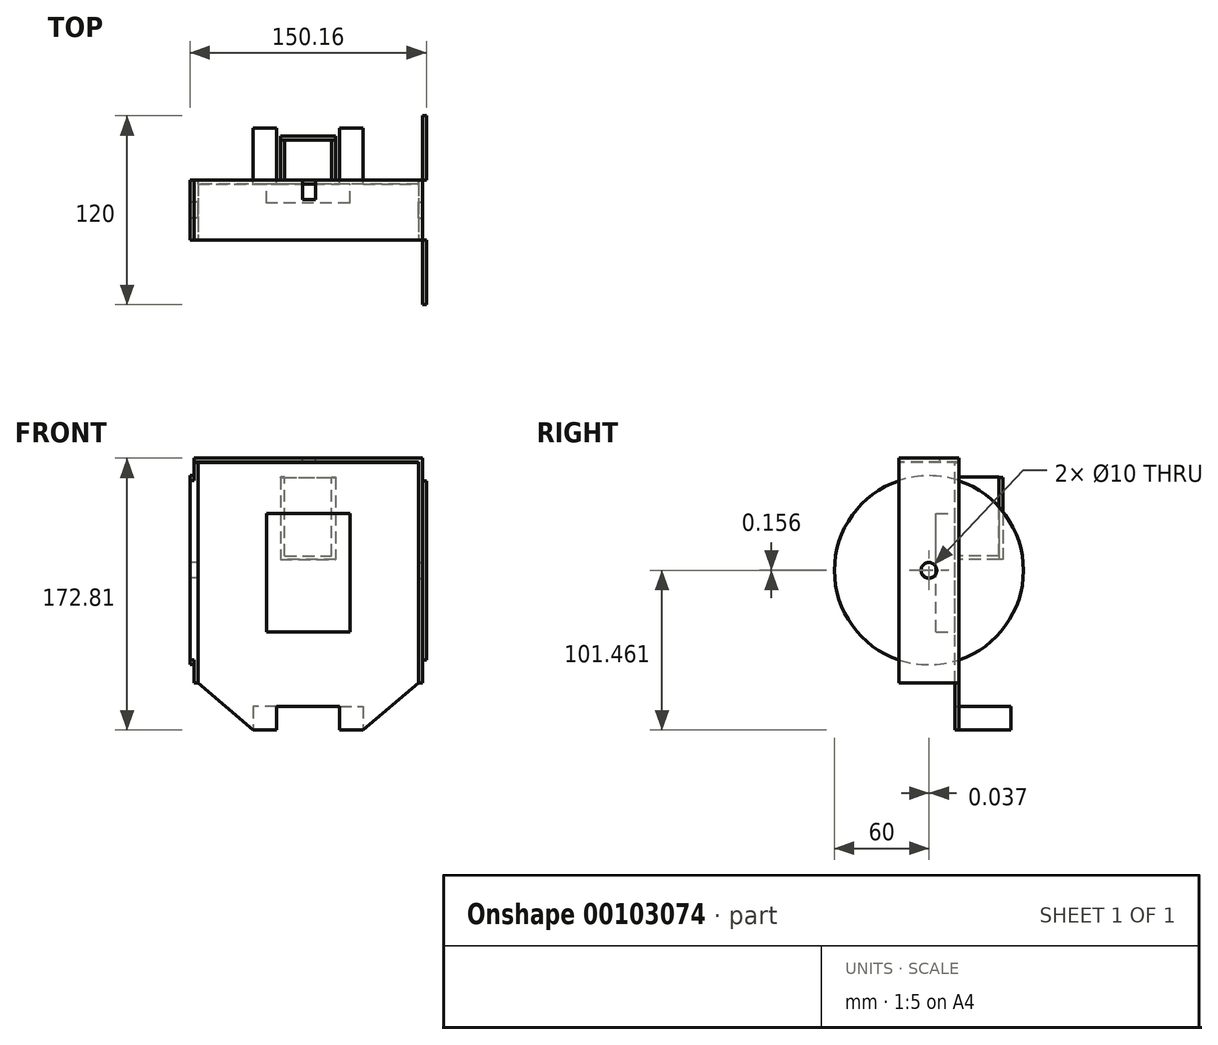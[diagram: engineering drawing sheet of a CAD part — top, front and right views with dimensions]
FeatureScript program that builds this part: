
annotation { "Feature Type Name" : "Feature", "Feature Type Description" : "" }
export const myFeature = defineFeature(function(context is Context, id is Id, definition is map)
    precondition{}
    {
        {
            var Q0;
            Q0=qCreatedBy(makeId("Front.planeOp"),FACE);
            var sketch = newSketch(context, id + "F0", { "sketchPlane" : qUnion([Q0])});
            skLineSegment(sketch, "E0.bottom", {"start": v(35, -85) * mm, "end": v(20, -85) * mm});
            skLineSegment(sketch, "E0.top", {"start": v(70, 85) * mm, "end": v(-70, 85) * mm});
            skLineSegment(sketch, "E0.left", {"start": v(70, -55) * mm, "end": v(70, 85) * mm});
            skLineSegment(sketch, "E0.right", {"start": v(-70, -55) * mm, "end": v(-70, 85) * mm});
            skPoint(sketch, "E0.middle", {"position": v(0, 0) * mm});
            skLineSegment(sketch, "E1", {"start": v(-70, -55) * mm, "end": v(-35, -85) * mm});
            skLineSegment(sketch, "E2", {"start": v(35, -85) * mm, "end": v(70, -55) * mm});
            skPoint(sketch, "E3.orphan", {"position": v(-70, -85) * mm});
            skPoint(sketch, "E4.orphan", {"position": v(70, -85) * mm});
            skLineSegment(sketch, "E5", {"start": v(-35, -85) * mm, "end": v(-20, -85) * mm});
            skLineSegment(sketch, "E6", {"start": v(-20, -85) * mm, "end": v(-20, -70) * mm});
            skLineSegment(sketch, "E7", {"start": v(20, -85) * mm, "end": v(20, -70) * mm});
            skLineSegment(sketch, "E8", {"start": v(-20, -70) * mm, "end": v(20, -70) * mm});
            skLineSegment(sketch, "E9.trimOffspring", {"start": v(-20, -85) * mm, "end": v(-35, -85) * mm});
            skSolve(sketch);
        }
        {
            var Q0;
            Q0=makeQuery(id+"F0.imprint","IMPRINT",FACE,{"disambiguationData":[TD([[makeQuery(id+"F0.imprint","IMPRINT",EDGE,{"derivedFrom":sQuery(id+"F0.wireOp",EDGE,"E0.top")}),1.0]])]});
            extrude(context, id + "F1", {"entities" : qUnion([Q0]), "depth" : 2.54 * mm});
        }
        {
            var Q0;
            Q0=makeQuery(id+"F1.opExtrude","CAP_FACE",FACE,{"disambiguationData":[OSD([sQuery(id+"F0.wireOp",EDGE,"E0.top"),sQuery(id+"F0.wireOp",EDGE,"E0.left"),sQuery(id+"F0.wireOp",EDGE,"E0.right"),sQuery(id+"F0.wireOp",EDGE,"E1"),sQuery(id+"F0.wireOp",EDGE,"E2"),sQuery(id+"F0.wireOp",EDGE,"E0.bottom"),sQuery(id+"F0.wireOp",EDGE,"E6"),sQuery(id+"F0.wireOp",EDGE,"E7"),sQuery(id+"F0.wireOp",EDGE,"E8"),sQuery(id+"F0.wireOp",EDGE,"E9.trimOffspring")])],"isStart":false});
            var sketch = newSketch(context, id + "F2", { "sketchPlane" : qUnion([Q0])});
            skLineSegment(sketch, "E10.bottom", {"start": v(26.5, -22.5) * mm, "end": v(-26.5, -22.5) * mm});
            skLineSegment(sketch, "E10.top", {"start": v(26.5, 52.5) * mm, "end": v(-26.5, 52.5) * mm});
            skLineSegment(sketch, "E10.left", {"start": v(26.5, -22.5) * mm, "end": v(26.5, 52.5) * mm});
            skLineSegment(sketch, "E10.right", {"start": v(-26.5, -22.5) * mm, "end": v(-26.5, 52.5) * mm});
            skPoint(sketch, "E10.middle", {"position": v(0, 15) * mm});
            skPoint(sketch, "E11.orphan", {"position": v(70, 85) * mm});
            skPoint(sketch, "E12.orphan", {"position": v(-70, -55) * mm});
            skSolve(sketch);
        }
        {
            var Q0;
            Q0=makeQuery(id+"F2.imprint","IMPRINT",FACE,{"disambiguationData":[TD([[makeQuery(id+"F2.imprint","IMPRINT",EDGE,{"derivedFrom":sQuery(id+"F2.wireOp",EDGE,"E10.bottom")}),-1.0]])]});
            extrude(context, id + "F3", {"entities" : qUnion([Q0]), "operationType" : NewBodyOperationType.ADD, "depth" : 12 * mm});
        }
        {
            var Q0;
            Q0=makeQuery(id+"F1.opExtrude","SWEPT_FACE",FACE,{"disambiguationData":[OSD([sQuery(id+"F0.wireOp",EDGE,"E0.right")])]});
            cPlane(context, id + "F4", {"entities" : qUnion([Q0]), "cplaneType" : CPlaneType.OFFSET, "offset" : 0 * mm, "width" : 152.4 * mm, "height" : 152.4 * mm});
        }
        {
            var Q0;
            Q0=qCreatedBy(id+"F4.planeOp",FACE);
            var sketch = newSketch(context, id + "F5", { "sketchPlane" : qUnion([Q0])});
            skLineSegment(sketch, "E13.bottom", {"start": v(0, 85.03) * mm, "end": v(38.1, 85.03) * mm});
            skLineSegment(sketch, "E13.top", {"start": v(0, -54.97) * mm, "end": v(38.1, -54.97) * mm});
            skLineSegment(sketch, "E13.left", {"start": v(0, 85.03) * mm, "end": v(0, -54.97) * mm});
            skLineSegment(sketch, "E13.right", {"start": v(38.1, 85.03) * mm, "end": v(38.1, -54.97) * mm});
            skSolve(sketch);
        }
        {
            var Q0;
            Q0=makeQuery(id+"F5.imprint","IMPRINT",FACE,{"disambiguationData":[TD([[makeQuery(id+"F5.imprint","IMPRINT",EDGE,{"derivedFrom":sQuery(id+"F5.wireOp",EDGE,"E13.bottom")}),-1.0]])]});
            extrude(context, id + "F6", {"entities" : qUnion([Q0]), "operationType" : NewBodyOperationType.ADD, "depth" : 2.54 * mm});
        }
        {
            var Q0;
            Q0=makeQuery(id+"F1.opExtrude","SWEPT_FACE",FACE,{"disambiguationData":[OSD([sQuery(id+"F0.wireOp",EDGE,"E0.left")])]});
            var Q1;
            Q1 = qBodyType(qCreatedBy(id + "F8" ,EDGE), BodyType.WIRE);
            cPlane(context, id + "F7", {"entities" : qUnion([Q0, Q1]), "cplaneType" : CPlaneType.OFFSET, "offset" : 0 * mm, "width" : 152.4 * mm, "height" : 152.4 * mm});
        }
        {
            var Q0;
            Q0=qCreatedBy(id+"F7.planeOp",FACE);
            var sketch = newSketch(context, id + "F8", { "sketchPlane" : qUnion([Q0])});
            skLineSegment(sketch, "E14.bottom", {"start": v(0, -54.89) * mm, "end": v(-38.1, -54.89) * mm});
            skLineSegment(sketch, "E14.top", {"start": v(0, 85.27) * mm, "end": v(-38.1, 85.27) * mm});
            skLineSegment(sketch, "E14.left", {"start": v(0, -54.89) * mm, "end": v(0, 85.27) * mm});
            skLineSegment(sketch, "E14.right", {"start": v(-38.1, -54.89) * mm, "end": v(-38.1, 85.27) * mm});
            skSolve(sketch);
        }
        {
            var Q0;
            Q0=makeQuery(id+"F8.imprint","IMPRINT",FACE,{"disambiguationData":[TD([[makeQuery(id+"F8.imprint","IMPRINT",EDGE,{"derivedFrom":sQuery(id+"F8.wireOp",EDGE,"E14.bottom")}),-1.0]])]});
            extrude(context, id + "F9", {"entities" : qUnion([Q0]), "operationType" : NewBodyOperationType.ADD, "depth" : 2.54 * mm});
        }
        {
            var Q0;
            Q0=makeQuery(id+"F9.boolean.opBoolean","MERGE",FACE,{"derivedFrom":[makeQuery(id+"F6.boolean.opBoolean","MERGE",FACE,{"derivedFrom":[makeQuery(id+"F1.opExtrude","CAP_FACE",FACE,{"disambiguationData":[OSD([sQuery(id+"F0.wireOp",EDGE,"E0.top"),sQuery(id+"F0.wireOp",EDGE,"E0.left"),sQuery(id+"F0.wireOp",EDGE,"E0.right"),sQuery(id+"F0.wireOp",EDGE,"E1"),sQuery(id+"F0.wireOp",EDGE,"E2"),sQuery(id+"F0.wireOp",EDGE,"E0.bottom"),sQuery(id+"F0.wireOp",EDGE,"E6"),sQuery(id+"F0.wireOp",EDGE,"E7"),sQuery(id+"F0.wireOp",EDGE,"E8"),sQuery(id+"F0.wireOp",EDGE,"E9.trimOffspring")])],"isStart":true}),makeQuery(id+"F6.opExtrude","SWEPT_FACE",FACE,{"disambiguationData":[OSD([sQuery(id+"F5.wireOp",EDGE,"E13.left")])]})]}),makeQuery(id+"F9.opExtrude","SWEPT_FACE",FACE,{"disambiguationData":[OSD([sQuery(id+"F8.wireOp",EDGE,"E14.left")])]})]});
            var sketch = newSketch(context, id + "F10", { "sketchPlane" : qUnion([Q0])});
            skLineSegment(sketch, "E15.bottom", {"start": v(-72.54, 85.27) * mm, "end": v(72.54, 85.27) * mm});
            skLineSegment(sketch, "E15.top", {"start": v(-72.54, 87.81) * mm, "end": v(72.54, 87.81) * mm});
            skLineSegment(sketch, "E15.left", {"start": v(-72.54, 85.27) * mm, "end": v(-72.54, 87.81) * mm});
            skLineSegment(sketch, "E15.right", {"start": v(72.54, 85.27) * mm, "end": v(72.54, 87.81) * mm});
            skSolve(sketch);
        }
        {
            var Q0;
            Q0=makeQuery(id+"F10.imprint","IMPRINT",FACE,{"disambiguationData":[TD([[makeQuery(id+"F10.imprint","IMPRINT",EDGE,{"derivedFrom":sQuery(id+"F10.wireOp",EDGE,"E15.top")}),-1.0]])]});
            extrude(context, id + "F11", {"entities" : qUnion([Q0]), "operationType" : NewBodyOperationType.ADD, "oppositeDirection" : true, "depth" : 38.1 * mm});
        }
        {
            var Q0;
            Q0=makeQuery(id+"F11.boolean.opBoolean","MERGE",FACE,{"derivedFrom":[makeQuery(id+"F9.boolean.opBoolean","MERGE",FACE,{"derivedFrom":[makeQuery(id+"F6.boolean.opBoolean","MERGE",FACE,{"derivedFrom":[makeQuery(id+"F1.opExtrude","CAP_FACE",FACE,{"disambiguationData":[OSD([sQuery(id+"F0.wireOp",EDGE,"E0.top"),sQuery(id+"F0.wireOp",EDGE,"E0.left"),sQuery(id+"F0.wireOp",EDGE,"E0.right"),sQuery(id+"F0.wireOp",EDGE,"E1"),sQuery(id+"F0.wireOp",EDGE,"E2"),sQuery(id+"F0.wireOp",EDGE,"E0.bottom"),sQuery(id+"F0.wireOp",EDGE,"E6"),sQuery(id+"F0.wireOp",EDGE,"E7"),sQuery(id+"F0.wireOp",EDGE,"E8"),sQuery(id+"F0.wireOp",EDGE,"E9.trimOffspring")])],"isStart":true}),makeQuery(id+"F6.opExtrude","SWEPT_FACE",FACE,{"disambiguationData":[OSD([sQuery(id+"F5.wireOp",EDGE,"E13.left")])]})]}),makeQuery(id+"F9.opExtrude","SWEPT_FACE",FACE,{"disambiguationData":[OSD([sQuery(id+"F8.wireOp",EDGE,"E14.left")])]})]}),makeQuery(id+"F11.opExtrude","CAP_FACE",FACE,{"disambiguationData":[OSD([sQuery(id+"F10.wireOp",EDGE,"E15.bottom"),sQuery(id+"F10.wireOp",EDGE,"E15.top"),sQuery(id+"F10.wireOp",EDGE,"E15.left"),sQuery(id+"F10.wireOp",EDGE,"E15.right")])],"isStart":true})]});
            var sketch = newSketch(context, id + "F12", { "sketchPlane" : qUnion([Q0])});
            skLineSegment(sketch, "E16.bottom", {"start": v(15, 25.68) * mm, "end": v(-15, 25.68) * mm});
            skLineSegment(sketch, "E16.top", {"start": v(15, 75.68) * mm, "end": v(-15, 75.68) * mm});
            skLineSegment(sketch, "E16.left", {"start": v(15, 25.68) * mm, "end": v(15, 75.68) * mm});
            skLineSegment(sketch, "E16.right", {"start": v(-15, 25.68) * mm, "end": v(-15, 75.68) * mm});
            skPoint(sketch, "E16.middle", {"position": v(0, 50.68) * mm});
            skLineSegment(sketch, "E17.bottom", {"start": v(15, 75.68) * mm, "end": v(17.54, 75.68) * mm});
            skLineSegment(sketch, "E17.left", {"start": v(15, 75.68) * mm, "end": v(15, 25.84) * mm});
            skLineSegment(sketch, "E17.right", {"start": v(17.54, 75.68) * mm, "end": v(17.54, 25.84) * mm});
            skLineSegment(sketch, "E18.bottom", {"start": v(-15, 75.68) * mm, "end": v(-17.54, 75.68) * mm});
            skLineSegment(sketch, "E18.left", {"start": v(-15, 75.68) * mm, "end": v(-15, 25.68) * mm});
            skLineSegment(sketch, "E18.right", {"start": v(-17.54, 75.68) * mm, "end": v(-17.54, 25.68) * mm});
            skLineSegment(sketch, "E19.bottom", {"start": v(-17.66, 79.83) * mm, "end": v(-17.87, 79.83) * mm});
            skLineSegment(sketch, "E19.top", {"start": v(-17.66, 80.87) * mm, "end": v(-17.87, 80.87) * mm});
            skLineSegment(sketch, "E19.left", {"start": v(-17.66, 79.83) * mm, "end": v(-17.66, 80.87) * mm});
            skLineSegment(sketch, "E19.right", {"start": v(-17.87, 79.83) * mm, "end": v(-17.87, 80.87) * mm});
            skLineSegment(sketch, "E20.bottom", {"start": v(-15, 25.68) * mm, "end": v(15, 25.68) * mm});
            skLineSegment(sketch, "E20.top", {"start": v(-17.54, 23.3) * mm, "end": v(17.54, 23.3) * mm});
            skLineSegment(sketch, "E20.left", {"start": v(-17.54, 25.68) * mm, "end": v(-17.54, 23.3) * mm});
            skLineSegment(sketch, "E20.right", {"start": v(17.54, 25.68) * mm, "end": v(17.54, 23.3) * mm});
            skLineSegment(sketch, "E21", {"start": v(-17.54, 75.68) * mm, "end": v(-17.54, 23.3) * mm});
            skLineSegment(sketch, "E22", {"start": v(17.54, 23.3) * mm, "end": v(17.54, 75.68) * mm});
            skSolve(sketch);
        }
        {
            var Q0;
            Q0=makeQuery(id+"F12.imprint","IMPRINT",FACE,{"disambiguationData":[TD([[makeQuery(id+"F12.imprint","IMPRINT",EDGE,{"derivedFrom":sQuery(id+"F12.wireOp",EDGE,"E16.left")}),-1.0]])]});
            extrude(context, id + "F13", {"entities" : qUnion([Q0]), "operationType" : NewBodyOperationType.ADD, "depth" : 25.4 * mm});
        }
        {
            var Q0;
            Q0=makeQuery(id+"F13.opExtrude","CAP_FACE",FACE,{"disambiguationData":[OSD([sQuery(id+"F12.wireOp",EDGE,"E16.left"),sQuery(id+"F12.wireOp",EDGE,"E17.bottom"),sQuery(id+"F12.wireOp",EDGE,"E17.left"),sQuery(id+"F12.wireOp",EDGE,"E18.bottom"),sQuery(id+"F12.wireOp",EDGE,"E18.left"),sQuery(id+"F12.wireOp",EDGE,"E20.bottom"),sQuery(id+"F12.wireOp",EDGE,"E20.top"),sQuery(id+"F12.wireOp",EDGE,"E21"),sQuery(id+"F12.wireOp",EDGE,"E22")])],"isStart":false});
            cPlane(context, id + "F14", {"entities" : qUnion([Q0]), "cplaneType" : CPlaneType.OFFSET, "offset" : 0 * mm, "width" : 152.4 * mm, "height" : 152.4 * mm});
        }
        {
            var Q0;
            Q0=qCreatedBy(id+"F14.planeOp",FACE);
            var sketch = newSketch(context, id + "F15", { "sketchPlane" : qUnion([Q0])});
            skLineSegment(sketch, "E23.bottom", {"start": v(17.55, 75.52) * mm, "end": v(-17.4, 75.52) * mm});
            skLineSegment(sketch, "E23.top", {"start": v(17.55, 23.41) * mm, "end": v(-17.4, 23.41) * mm});
            skLineSegment(sketch, "E23.left", {"start": v(17.55, 75.52) * mm, "end": v(17.55, 23.41) * mm});
            skLineSegment(sketch, "E23.right", {"start": v(-17.4, 75.52) * mm, "end": v(-17.4, 23.41) * mm});
            skSolve(sketch);
        }
        {
            var Q0;
            Q0=makeQuery(id+"F15.imprint","IMPRINT",FACE,{"disambiguationData":[TD([[makeQuery(id+"F15.imprint","IMPRINT",EDGE,{"derivedFrom":sQuery(id+"F15.wireOp",EDGE,"E23.bottom")}),1.0]])]});
            extrude(context, id + "F16", {"entities" : qUnion([Q0]), "operationType" : NewBodyOperationType.ADD, "depth" : 2.54 * mm});
        }
        {
            var Q0;
            Q0=makeQuery(id+"F11.opExtrude","SWEPT_FACE",FACE,{"disambiguationData":[OSD([sQuery(id+"F10.wireOp",EDGE,"E15.top")])]});
            var sketch = newSketch(context, id + "F17", { "sketchPlane" : qUnion([Q0])});
            skLineSegment(sketch, "E24.bottom", {"start": v(-3.47, 0) * mm, "end": v(4.72, 0) * mm});
            skLineSegment(sketch, "E24.top", {"start": v(-3.47, -12.2) * mm, "end": v(4.72, -12.2) * mm});
            skLineSegment(sketch, "E24.left", {"start": v(-3.47, 0) * mm, "end": v(-3.47, -12.2) * mm});
            skLineSegment(sketch, "E24.right", {"start": v(4.72, 0) * mm, "end": v(4.72, -12.2) * mm});
            skSolve(sketch);
        }
        {
            var Q0;
            Q0=makeQuery(id+"F17.imprint","IMPRINT",FACE,{"disambiguationData":[TD([[makeQuery(id+"F17.imprint","IMPRINT",EDGE,{"derivedFrom":sQuery(id+"F17.wireOp",EDGE,"E24.bottom")}),1.0]])]});
            extrude(context, id + "F18", {"entities" : qUnion([Q0]), "operationType" : NewBodyOperationType.REMOVE, "oppositeDirection" : true, "depth" : 2.54 * mm});
        }
        {
            var Q0;
            Q0=makeQuery(id+"F11.boolean.opBoolean","MERGE",FACE,{"derivedFrom":[makeQuery(id+"F9.opExtrude","CAP_FACE",FACE,{"disambiguationData":[OSD([sQuery(id+"F8.wireOp",EDGE,"E14.bottom"),sQuery(id+"F8.wireOp",EDGE,"E14.top"),sQuery(id+"F8.wireOp",EDGE,"E14.left"),sQuery(id+"F8.wireOp",EDGE,"E14.right")])],"isStart":false}),makeQuery(id+"F11.opExtrude","SWEPT_FACE",FACE,{"disambiguationData":[OSD([sQuery(id+"F10.wireOp",EDGE,"E15.left")])]})]});
            var sketch = newSketch(context, id + "F19", { "sketchPlane" : qUnion([Q0])});
            skCircle(sketch, "E25", {"center": v(-19.05, 16.46) * mm, "radius": 5 * mm});
            skSolve(sketch);
        }
        {
            var Q0;
            Q0=makeQuery(id+"F19.imprint","IMPRINT",FACE,{"disambiguationData":[TD([[makeQuery(id+"F19.imprint","IMPRINT",EDGE,{"derivedFrom":sQuery(id+"F19.wireOp",EDGE,"E25")}),1.0]])]});
            extrude(context, id + "F20", {"entities" : qUnion([Q0]), "operationType" : NewBodyOperationType.REMOVE, "oppositeDirection" : true, "depth" : 5.08 * mm});
        }
        {
            var Q0;
            Q0=makeQuery(id+"F6.opExtrude","CAP_FACE",FACE,{"disambiguationData":[OSD([sQuery(id+"F5.wireOp",EDGE,"E13.bottom"),sQuery(id+"F5.wireOp",EDGE,"E13.top"),sQuery(id+"F5.wireOp",EDGE,"E13.left"),sQuery(id+"F5.wireOp",EDGE,"E13.right")])],"isStart":false});
            var sketch = newSketch(context, id + "F21", { "sketchPlane" : qUnion([Q0])});
            skCircle(sketch, "E26", {"center": v(19.01, 16.62) * mm, "radius": 5 * mm});
            skSolve(sketch);
        }
        {
            var Q0;
            Q0=makeQuery(id+"F21.imprint","IMPRINT",FACE,{"disambiguationData":[TD([[makeQuery(id+"F21.imprint","IMPRINT",EDGE,{"derivedFrom":sQuery(id+"F21.wireOp",EDGE,"E26")}),1.0]])]});
            extrude(context, id + "F22", {"entities" : qUnion([Q0]), "operationType" : NewBodyOperationType.REMOVE, "oppositeDirection" : true, "depth" : 5.08 * mm});
        }
        {
            var Q0;
            Q0=makeQuery(id+"F6.opExtrude","CAP_FACE",FACE,{"disambiguationData":[OSD([sQuery(id+"F5.wireOp",EDGE,"E13.bottom"),sQuery(id+"F5.wireOp",EDGE,"E13.top"),sQuery(id+"F5.wireOp",EDGE,"E13.left"),sQuery(id+"F5.wireOp",EDGE,"E13.right")])],"isStart":false});
            var sketch = newSketch(context, id + "F23", { "sketchPlane" : qUnion([Q0])});
            skCircle(sketch, "E27", {"center": v(19.01, 16.62) * mm, "radius": 60 * mm});
            skSolve(sketch);
        }
        {
            var Q0;
            Q0=makeQuery(id+"F11.boolean.opBoolean","MERGE",FACE,{"derivedFrom":[makeQuery(id+"F9.opExtrude","CAP_FACE",FACE,{"disambiguationData":[OSD([sQuery(id+"F8.wireOp",EDGE,"E14.bottom"),sQuery(id+"F8.wireOp",EDGE,"E14.top"),sQuery(id+"F8.wireOp",EDGE,"E14.left"),sQuery(id+"F8.wireOp",EDGE,"E14.right")])],"isStart":false}),makeQuery(id+"F11.opExtrude","SWEPT_FACE",FACE,{"disambiguationData":[OSD([sQuery(id+"F10.wireOp",EDGE,"E15.left")])]})]});
            var sketch = newSketch(context, id + "F24", { "sketchPlane" : qUnion([Q0])});
            skCircle(sketch, "E28", {"center": v(-19.05, 16.46) * mm, "radius": 60 * mm});
            skSolve(sketch);
        }
        {
            var Q0;
            {var subQ0=sQuery(id+"F24.wireOp",EDGE,"E28");var subQ1=makeQuery(id+"F11.boolean.opBoolean","MERGE",EDGE,{"derivedFrom":[makeQuery(id+"F9.opExtrude","CAP_EDGE",EDGE,{"disambiguationData":[OSD([sQuery(id+"F8.wireOp",EDGE,"E14.left")])],"isStart":false}),makeQuery(id+"F11.opExtrude","CAP_EDGE",EDGE,{"disambiguationData":[OSD([sQuery(id+"F10.wireOp",EDGE,"E15.left")])],"isStart":true})]});var subQ2=makeQuery(id+"F24.imprint","INTERSECT",VERTEX,{"disambiguationData":[OD(0.0)],"derivedFrom":[subQ1,subQ0]});Q0=makeQuery(id+"F24.imprint","IMPRINT",FACE,{"disambiguationData":[TD([[makeQuery(id+"F24.imprint","IMPRINT",EDGE,{"disambiguationData":[TD([[subQ2,1.0]])],"derivedFrom":subQ0}),1.0]])]});}
            var Q1;
            {var subQ0=sQuery(id+"F24.wireOp",EDGE,"E28");var subQ1=makeQuery(id+"F11.boolean.opBoolean","MERGE",EDGE,{"derivedFrom":[makeQuery(id+"F9.opExtrude","CAP_EDGE",EDGE,{"disambiguationData":[OSD([sQuery(id+"F8.wireOp",EDGE,"E14.right")])],"isStart":false}),makeQuery(id+"F11.opExtrude","CAP_EDGE",EDGE,{"disambiguationData":[OSD([sQuery(id+"F10.wireOp",EDGE,"E15.left")])],"isStart":false})]});var subQ2=makeQuery(id+"F24.imprint","INTERSECT",VERTEX,{"disambiguationData":[OD(0.0)],"derivedFrom":[subQ1,subQ0]});Q1=makeQuery(id+"F24.imprint","IMPRINT",FACE,{"disambiguationData":[TD([[makeQuery(id+"F24.imprint","IMPRINT",EDGE,{"disambiguationData":[TD([[subQ2,-1.0]])],"derivedFrom":subQ0}),1.0]])]});}
            var Q2;
            Q2=makeQuery(id+"F24.imprint","IMPRINT",FACE,{"disambiguationData":[TD([[makeQuery(id+"F24.imprint","IMPRINT",EDGE,{"derivedFrom":makeQuery(id+"F20.boolean.opBoolean","COPY",EDGE,{"derivedFrom":makeQuery(id+"F20.opExtrude","CAP_EDGE",EDGE,{"disambiguationData":[OSD([sQuery(id+"F19.wireOp",EDGE,"E25")])],"isStart":true})})}),-1.0]])]});
            extrude(context, id + "F25", {"entities" : qUnion([Q0, Q1, Q2]), "operationType" : NewBodyOperationType.ADD, "depth" : 2.54 * mm});
        }
        {
            var Q0;
            {var subQ0=sQuery(id+"F23.wireOp",EDGE,"E27");var subQ1=makeQuery(id+"F6.opExtrude","CAP_EDGE",EDGE,{"disambiguationData":[OSD([sQuery(id+"F5.wireOp",EDGE,"E13.left")])],"isStart":false});var subQ2=makeQuery(id+"F23.imprint","INTERSECT",VERTEX,{"disambiguationData":[OD(0.0)],"derivedFrom":[subQ1,subQ0]});Q0=makeQuery(id+"F23.imprint","IMPRINT",FACE,{"disambiguationData":[TD([[makeQuery(id+"F23.imprint","IMPRINT",EDGE,{"disambiguationData":[TD([[subQ2,-1.0]])],"derivedFrom":subQ0}),1.0]])]});}
            var Q1;
            {var subQ0=sQuery(id+"F23.wireOp",EDGE,"E27");var subQ1=makeQuery(id+"F6.opExtrude","CAP_EDGE",EDGE,{"disambiguationData":[OSD([sQuery(id+"F5.wireOp",EDGE,"E13.right")])],"isStart":false});var subQ2=makeQuery(id+"F23.imprint","INTERSECT",VERTEX,{"disambiguationData":[OD(0.0)],"derivedFrom":[subQ1,subQ0]});Q1=makeQuery(id+"F23.imprint","IMPRINT",FACE,{"disambiguationData":[TD([[makeQuery(id+"F23.imprint","IMPRINT",EDGE,{"disambiguationData":[TD([[subQ2,1.0]])],"derivedFrom":subQ0}),1.0]])]});}
            var Q2;
            Q2=makeQuery(id+"F23.imprint","IMPRINT",FACE,{"disambiguationData":[TD([[makeQuery(id+"F23.imprint","IMPRINT",EDGE,{"derivedFrom":makeQuery(id+"F22.boolean.opBoolean","COPY",EDGE,{"derivedFrom":makeQuery(id+"F22.opExtrude","CAP_EDGE",EDGE,{"disambiguationData":[OSD([sQuery(id+"F21.wireOp",EDGE,"E26")])],"isStart":true})})}),-1.0]])]});
            extrude(context, id + "F26", {"entities" : qUnion([Q0, Q1, Q2]), "operationType" : NewBodyOperationType.ADD, "depth" : 2.54 * mm});
        }
        {
            var Q0;
            {var subQ0=sQuery(id+"F10.wireOp",EDGE,"E15.left");var subQ1=sQuery(id+"F0.wireOp",EDGE,"E6");var subQ3=sQuery(id+"F8.wireOp",EDGE,"E14.left");var subQ6=sQuery(id+"F10.wireOp",EDGE,"E15.bottom");var subQ9=sQuery(id+"F5.wireOp",EDGE,"E13.left");var subQ11=sQuery(id+"F0.wireOp",EDGE,"E1");var subQ12=sQuery(id+"F0.wireOp",EDGE,"E0.right");var subQ13=sQuery(id+"F0.wireOp",EDGE,"E0.left");var subQ14=sQuery(id+"F0.wireOp",EDGE,"E8");var subQ15=sQuery(id+"F0.wireOp",EDGE,"E0.top");var subQ16=sQuery(id+"F0.wireOp",EDGE,"E2");var subQ17=sQuery(id+"F0.wireOp",EDGE,"E0.bottom");var subQ18=sQuery(id+"F10.wireOp",EDGE,"E15.top");var subQ19=sQuery(id+"F0.wireOp",EDGE,"E7");var subQ20=sQuery(id+"F0.wireOp",EDGE,"E9.trimOffspring");Q0=makeQuery(id+"F18.boolean.opBoolean","SPLIT",FACE,{"disambiguationData":[TD([makeQuery(id+"F1.opExtrude","SWEPT_FACE",FACE,{"disambiguationData":[OSD([subQ15])]})])],"derivedFrom":makeQuery(id+"F11.boolean.opBoolean","MERGE",FACE,{"derivedFrom":[makeQuery(id+"F9.boolean.opBoolean","MERGE",FACE,{"derivedFrom":[makeQuery(id+"F6.boolean.opBoolean","MERGE",FACE,{"derivedFrom":[makeQuery(id+"F1.opExtrude","CAP_FACE",FACE,{"disambiguationData":[OSD([subQ15,subQ13,subQ12,subQ11,subQ16,subQ17,subQ1,subQ19,subQ14,subQ20])],"isStart":true}),makeQuery(id+"F6.opExtrude","SWEPT_FACE",FACE,{"disambiguationData":[OSD([subQ9])]})]}),makeQuery(id+"F9.opExtrude","SWEPT_FACE",FACE,{"disambiguationData":[OSD([subQ3])]})]}),makeQuery(id+"F11.opExtrude","CAP_FACE",FACE,{"disambiguationData":[OSD([subQ6,subQ18,subQ0,sQuery(id+"F10.wireOp",EDGE,"E15.right")])],"isStart":true})]})});}
            var sketch = newSketch(context, id + "F27", { "sketchPlane" : qUnion([Q0])});
            skLineSegment(sketch, "E29.bottom", {"start": v(-20, -70) * mm, "end": v(-35, -70) * mm});
            skLineSegment(sketch, "E29.top", {"start": v(-20, -85) * mm, "end": v(-35, -85) * mm});
            skLineSegment(sketch, "E29.left", {"start": v(-20, -70) * mm, "end": v(-20, -85) * mm});
            skLineSegment(sketch, "E29.right", {"start": v(-35, -70) * mm, "end": v(-35, -85) * mm});
            skLineSegment(sketch, "E30.bottom", {"start": v(20, -70) * mm, "end": v(35, -70) * mm});
            skLineSegment(sketch, "E30.top", {"start": v(20, -85) * mm, "end": v(35, -85) * mm});
            skLineSegment(sketch, "E30.left", {"start": v(20, -70) * mm, "end": v(20, -85) * mm});
            skLineSegment(sketch, "E30.right", {"start": v(35, -70) * mm, "end": v(35, -85) * mm});
            skSolve(sketch);
        }
        {
            var Q0;
            Q0=makeQuery(id+"F27.imprint","IMPRINT",FACE,{"disambiguationData":[TD([[makeQuery(id+"F27.imprint","IMPRINT",EDGE,{"derivedFrom":sQuery(id+"F27.wireOp",EDGE,"E29.bottom")}),1.0]])]});
            var Q1;
            Q1=makeQuery(id+"F27.imprint","IMPRINT",FACE,{"disambiguationData":[TD([[makeQuery(id+"F27.imprint","IMPRINT",EDGE,{"derivedFrom":sQuery(id+"F27.wireOp",EDGE,"E30.bottom")}),-1.0]])]});
            extrude(context, id + "F28", {"entities" : qUnion([Q0, Q1]), "operationType" : NewBodyOperationType.ADD, "depth" : 33.02 * mm});
        }
    });
